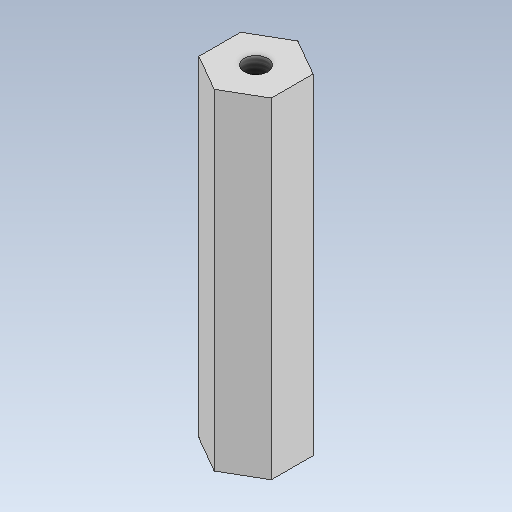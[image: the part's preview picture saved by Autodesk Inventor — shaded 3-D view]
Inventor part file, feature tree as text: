
AUTODESK INVENTOR PART (.ipt)
format: ipt  version: 2023 (Build 270158000, 158)  size: 105,472 bytes
history: native  units: in
note: dims shown in document units (in); Inventor stores cm internally (conversion verified against a paired STEP export)
features: sketch x3, hole x2, extrude x1
ambient origin geometry x8: Origin, YZ Plane, XZ Plane, XY Plane, X Axis, Y Axis, Z Axis, Center Point
bodies: Solid1 (feature_tree)
feature tree (6):
  extrude  "Extrusion1"  Depth=2.2835in TaperAngle=0.0deg
  hole  "Hole1"  [1 undecoded]
  hole  "Hole2"  [1 undecoded]
  sketch  "Sketch1"  dims[d0=0.25in d1=2.2835in d2=0.0in]
  sketch  "Sketch3"  dims[d3=0.1628in d4=0.3937in d5=0.1575in d6=0.0787in d7=90.0deg d8=0.5118in d9=0.8108in]
  sketch  "Sketch4"  dims[d10=0.1628in d11=0.5118in d12=0.1575in d13=0.0787in d14=90.0deg d15=0.5118in d16=0.8108in]
note: 2 required parameter values undecoded (feature->parameter linkage not recoverable at this tier; creation-order binding heuristic only, values carry confidence <= 0.55)
